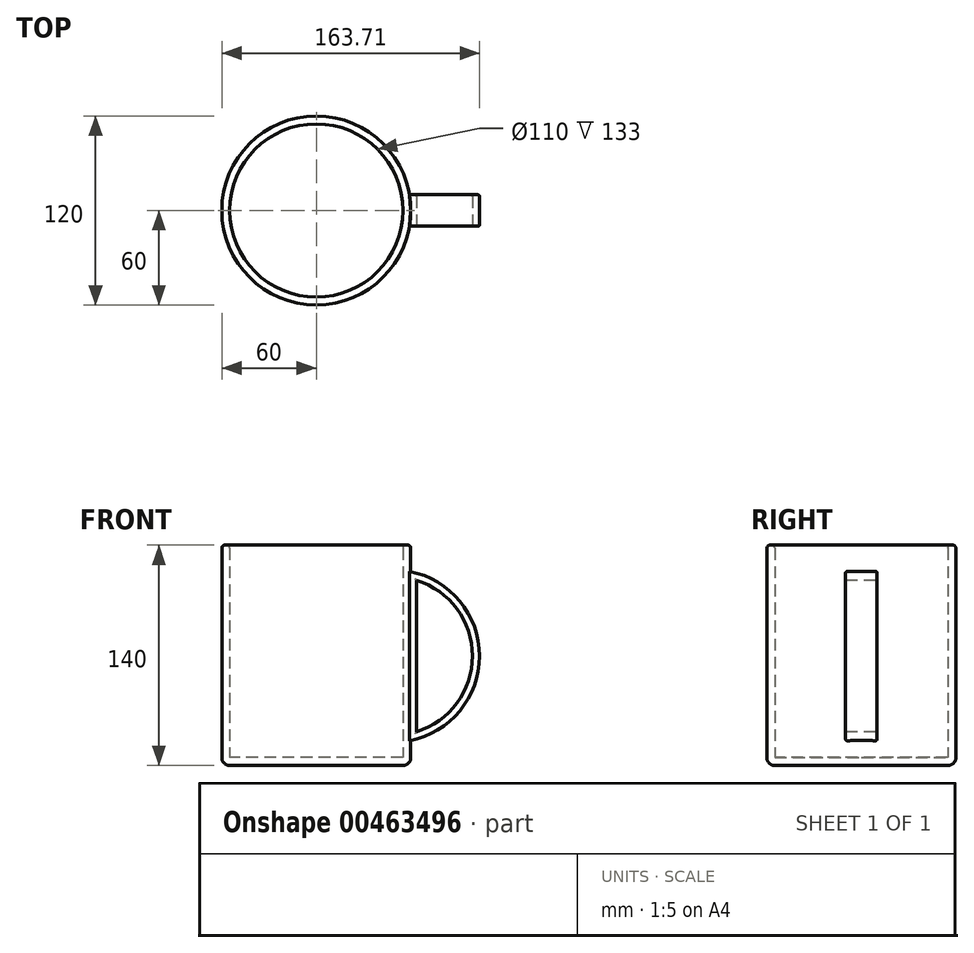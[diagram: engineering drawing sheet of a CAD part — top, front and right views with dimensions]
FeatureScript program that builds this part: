
annotation { "Feature Type Name" : "Feature", "Feature Type Description" : "" }
export const myFeature = defineFeature(function(context is Context, id is Id, definition is map)
    precondition{}
    {
        {
            var Q0;
            Q0=qCreatedBy(makeId("Top.planeOp"),FACE);
            var sketch = newSketch(context, id + "F0", { "sketchPlane" : qUnion([Q0])});
            skCircle(sketch, "E0", {"center": v(0, 0) * mm, "radius": 60 * mm});
            skSolve(sketch);
        }
        {
            var Q0;
            Q0 = qSketchRegion(id + "F0", true);
            extrude(context, id + "F1", {"entities" : qUnion([Q0]), "depth" : 140 * mm});
        }
        {
            var Q0;
            Q0=makeQuery(id+"F1.opExtrude","CAP_FACE",FACE,{"disambiguationData":[OSD([sQuery(id+"F0.wireOp",EDGE,"E0")])],"isStart":false});
            shell(context, id + "F2", {"entities" : qUnion([Q0]), "thickness" : 5 * mm});
        }
        {
            var Q0;
            {var subQ0=sQuery(id+"F0.wireOp",EDGE,"E0");Q0=makeQuery(id+"F2.opShell","OFFSET_EDGE",EDGE,{"disambiguationData":[OSD([subQ0]),TDD([makeQuery(id+"F1.opExtrude","CAP_EDGE",EDGE,{"disambiguationData":[OSD([subQ0])],"isStart":false})])]});}
            var Q1;
            Q1=makeQuery(id+"F1.opExtrude","CAP_EDGE",EDGE,{"disambiguationData":[OSD([sQuery(id+"F0.wireOp",EDGE,"E0")])],"isStart":false});
            fillet(context, id + "F3", {"entities" : qUnion([Q0, Q1]), "radius" : 2 * mm, "tangentPropagation" : true, "allowEdgeOverflow" : false});
        }
        {
            var Q0;
            Q0=qCreatedBy(makeId("Front.planeOp"),FACE);
            var sketch = newSketch(context, id + "F4", { "sketchPlane" : qUnion([Q0])});
            skArc(sketch, "E1", {"start": v(57.76, 15.44) * mm, "mid": v(103.71, 69.47) * mm, "end": v(57.76, 123.5) * mm});
            skPoint(sketch, "E1.second.point", {"position": v(61.87, 16.27) * mm});
            skLineSegment(sketch, "E2", {"start": v(57.76, 15.44) * mm, "end": v(57.76, 123.5) * mm});
            skSolve(sketch);
        }
        {
            var Q0;
            Q0 = qSketchRegion(id + "F4", true);
            extrude(context, id + "F5", {"entities" : qUnion([Q0]), "operationType" : NewBodyOperationType.ADD, "endBound" : BoundingType.SYMMETRIC, "depth" : 20 * mm});
        }
        {
            var Q0;
            Q0=makeQuery(id+"F5.opExtrude","CAP_FACE",FACE,{"disambiguationData":[OSD([sQuery(id+"F4.wireOp",EDGE,"E1"),sQuery(id+"F4.wireOp",EDGE,"E2")])],"isStart":false});
            var sketch = newSketch(context, id + "F6", { "sketchPlane" : qUnion([Q0])});
            skLineSegment(sketch, "E3.0", {"start": v(63.66, 21.43) * mm, "end": v(63.66, 117.52) * mm});
            skArc(sketch, "E3.1", {"start": v(63.66, 21.43) * mm, "mid": v(99.21, 69.47) * mm, "end": v(63.66, 117.52) * mm});
            skSolve(sketch);
        }
        {
            var Q0;
            Q0=makeQuery(id+"F6.imprint","IMPRINT",FACE,{"disambiguationData":[TD([[makeQuery(id+"F6.imprint","IMPRINT",EDGE,{"derivedFrom":sQuery(id+"F6.wireOp",EDGE,"E3.0")}),-1.0]])]});
            extrude(context, id + "F7", {"entities" : qUnion([Q0]), "operationType" : NewBodyOperationType.REMOVE, "oppositeDirection" : true, "depth" : 54 * mm});
        }
        {
            var Q0;
            Q0=makeQuery(id+"F7.boolean.opBoolean","COPY",EDGE,{"derivedFrom":makeQuery(id+"F7.opExtrude","CAP_EDGE",EDGE,{"disambiguationData":[OSD([sQuery(id+"F6.wireOp",EDGE,"E3.1")])],"isStart":true})});
            var Q1;
            Q1=makeQuery(id+"F7.boolean.opBoolean","COPY",EDGE,{"derivedFrom":makeQuery(id+"F7.opExtrude","CAP_EDGE",EDGE,{"disambiguationData":[OSD([sQuery(id+"F6.wireOp",EDGE,"E3.0")])],"isStart":true})});
            var Q2;
            Q2=makeQuery(id+"F7.boolean.opBoolean","INTERSECT",EDGE,{"derivedFrom":[makeQuery(id+"F5.opExtrude","CAP_FACE",FACE,{"disambiguationData":[OSD([sQuery(id+"F4.wireOp",EDGE,"E1"),sQuery(id+"F4.wireOp",EDGE,"E2")])],"isStart":true}),makeQuery(id+"F7.opExtrude","SWEPT_FACE",FACE,{"disambiguationData":[OSD([sQuery(id+"F6.wireOp",EDGE,"E3.0")])]})]});
            var Q3;
            Q3=makeQuery(id+"F7.boolean.opBoolean","INTERSECT",EDGE,{"derivedFrom":[makeQuery(id+"F5.opExtrude","CAP_FACE",FACE,{"disambiguationData":[OSD([sQuery(id+"F4.wireOp",EDGE,"E1"),sQuery(id+"F4.wireOp",EDGE,"E2")])],"isStart":true}),makeQuery(id+"F7.opExtrude","SWEPT_FACE",FACE,{"disambiguationData":[OSD([sQuery(id+"F6.wireOp",EDGE,"E3.1")])]})]});
            var Q4;
            Q4=makeQuery(id+"F5.opExtrude","CAP_EDGE",EDGE,{"disambiguationData":[OSD([sQuery(id+"F4.wireOp",EDGE,"E1")])],"isStart":true});
            var Q5;
            Q5=makeQuery(id+"F5.opExtrude","CAP_EDGE",EDGE,{"disambiguationData":[OSD([sQuery(id+"F4.wireOp",EDGE,"E1")])],"isStart":false});
            fillet(context, id + "F8", {"entities" : qUnion([Q0, Q1, Q2, Q3, Q4, Q5]), "radius" : 1 * mm, "tangentPropagation" : true, "allowEdgeOverflow" : false});
        }
        {
            var Q0;
            Q0=makeQuery(id+"F1.opExtrude","CAP_EDGE",EDGE,{"disambiguationData":[OSD([sQuery(id+"F0.wireOp",EDGE,"E0")])],"isStart":true});
            fillet(context, id + "F9", {"entities" : qUnion([Q0]), "radius" : 5 * mm, "tangentPropagation" : true, "allowEdgeOverflow" : false});
        }
    });
